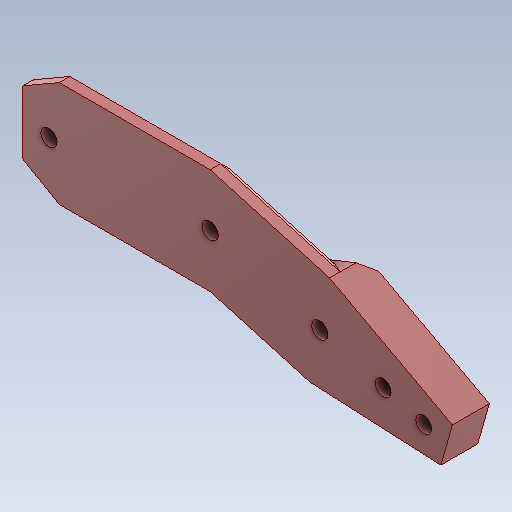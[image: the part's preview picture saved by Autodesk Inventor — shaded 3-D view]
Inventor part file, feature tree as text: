
AUTODESK INVENTOR PART (.ipt)
format: ipt  version: 2020 (Build 240168000, 168)  size: 218,624 bytes
history: native  units: in
note: dims shown in document units (in); Inventor stores cm internally (conversion verified against a paired STEP export)
features: extrude x3, sketch x3, projected_geometry x2, chamfer x1
ambient origin geometry x8: Origin, YZ Plane, XZ Plane, XY Plane, X Axis, Y Axis, Z Axis, Center Point
bodies: Solid1 (feature_tree)
feature tree (9):
  extrude  "Extrusion1"  Depth=1.2027in
  extrude  "Extrusion2"  Depth=1.1274in
  extrude  "Extrusion3"  Depth=0.0787in
  chamfer  "Chamfer1"  Distance=0.1969in
  sketch  "Sketch1"  dims[d0=0.122in d1=1.2027in]
  sketch  "Sketch3"  dims[d2=0.122in d3=1.1274in]
  projected_geometry  "Projected Loop2"
  sketch  "Sketch4"  dims[d4=0.122in d5=0.8503in d6=0.1969in d7=0.2362in d8=0.2362in d9=120.0deg d10=0.315in d11=120.0deg d12=0.315in d13=1.1268in d14=1.1268in d15=0.7744in d16=0.9262in d19=0.1575in d20=0.0in d23=0.0759in d54=0.9843in d55=180.0deg d56=0.1575in d57=0.1575in d58=90.0deg d59=90.0deg d60=0.1181in d61=0.315in d62=0.1181in d63=0.3937in d64=0.3937in d65=0.8933in d66=135.0deg d67=0.2756in d68=0.0in d69=0.2205in d70=0.2205in d71=0.2205in d72=0.0787in d73=0.0in d74=0.0787in d75=0.0787in d76=45.0deg]
  projected_geometry  "Projected Loop3"
